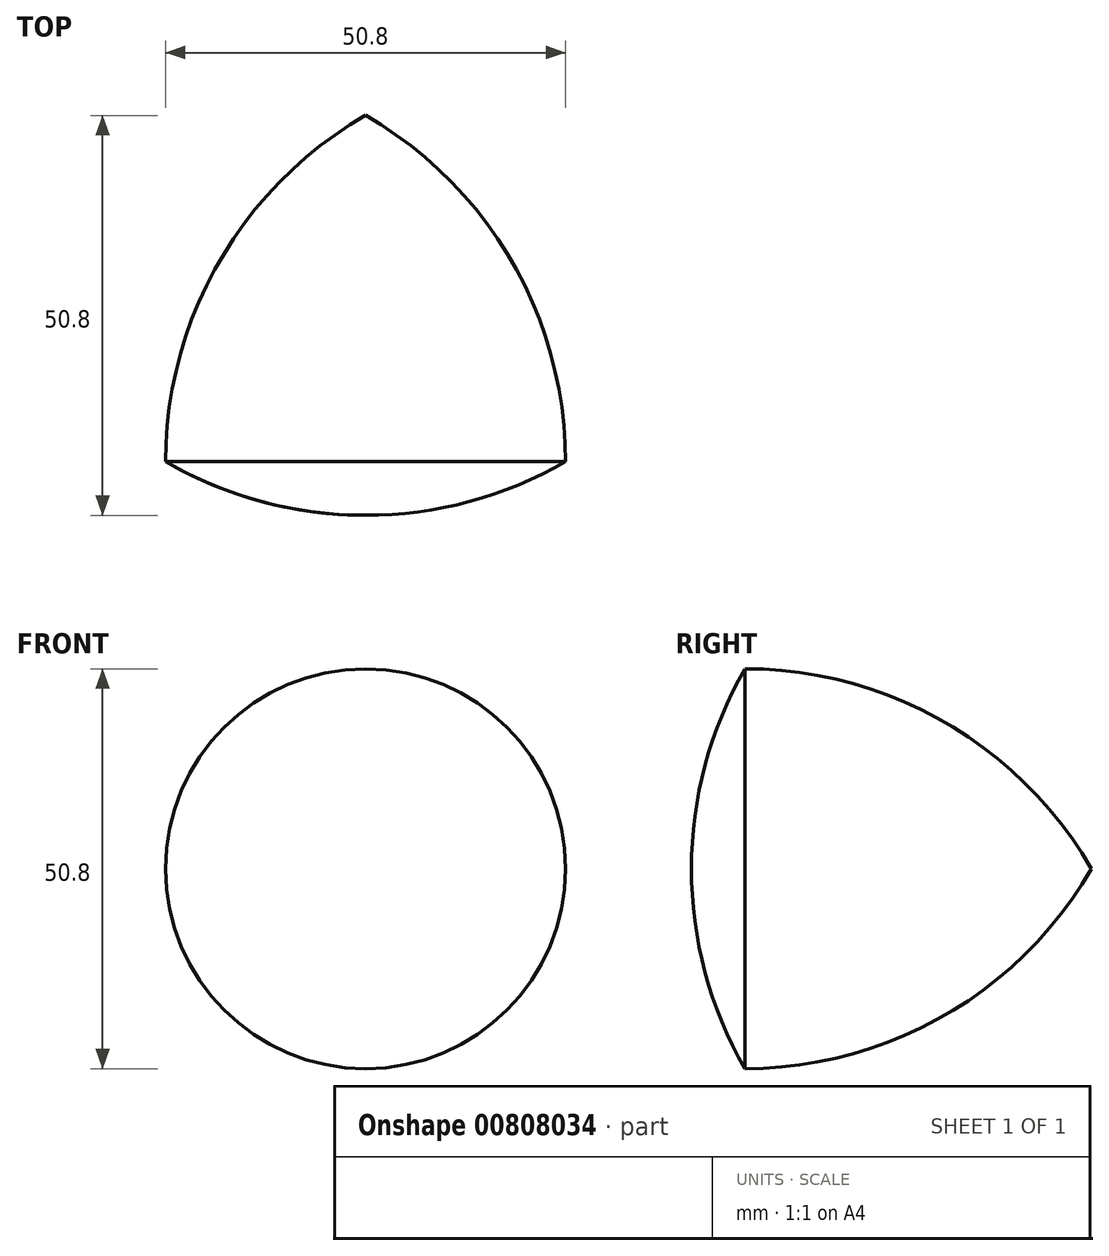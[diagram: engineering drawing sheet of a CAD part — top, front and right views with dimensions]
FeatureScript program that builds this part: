
annotation { "Feature Type Name" : "Feature", "Feature Type Description" : "" }
export const myFeature = defineFeature(function(context is Context, id is Id, definition is map)
    precondition{}
    {
        {
            var Q0;
            Q0=qCreatedBy(makeId("Top.planeOp"),FACE);
            var sketch = newSketch(context, id + "F0", { "sketchPlane" : qUnion([Q0])});
            skLineSegment(sketch, "E0", {"start": v(-25.4, 0) * mm, "end": v(25.4, 0) * mm});
            skLineSegment(sketch, "E1", {"start": v(25.4, 0) * mm, "end": v(0, 44) * mm});
            skLineSegment(sketch, "E2", {"start": v(0, 44) * mm, "end": v(-25.4, 0) * mm});
            skCircle(sketch, "E3", {"center": v(-25.4, 0) * mm, "radius": 50.8 * mm});
            skPoint(sketch, "E3.third.point", {"position": v(-71.73, -20.83) * mm});
            skCircle(sketch, "E4", {"center": v(25.4, 0) * mm, "radius": 50.8 * mm});
            skPoint(sketch, "E4.third.point", {"position": v(67.6, -28.28) * mm});
            skCircle(sketch, "E5", {"center": v(0, 44) * mm, "radius": 50.8 * mm});
            skPoint(sketch, "E5.third.point", {"position": v(0, 94.8) * mm});
            skCircle(sketch, "E6", {"center": v(0, 14.66) * mm, "radius": 29.33 * mm});
            skLineSegment(sketch, "E7", {"start": v(0, 44) * mm, "end": v(0, 0) * mm});
            skLineSegment(sketch, "E8", {"start": v(0, 44) * mm, "end": v(0, -6.8) * mm});
            skSolve(sketch);
        }
        {
            var Q0;
            {var subQ0=sQuery(id+"F0.wireOp",EDGE,"E2");Q0=makeQuery(id+"F0.imprint","IMPRINT",FACE,{"disambiguationData":[TD([[makeQuery(id+"F0.imprint","IMPRINT",EDGE,{"derivedFrom":subQ0}),-1.0]])]});}
            var Q1;
            {var subQ0=sQuery(id+"F0.wireOp",EDGE,"E2");Q1=makeQuery(id+"F0.imprint","IMPRINT",FACE,{"disambiguationData":[TD([[makeQuery(id+"F0.imprint","IMPRINT",EDGE,{"derivedFrom":subQ0}),1.0]])]});}
            var Q2;
            {var subQ2=sQuery(id+"F0.wireOp",EDGE,"E0");var subQ4=makeQuery(id+"F0.imprint","INTERSECT",VERTEX,{"derivedFrom":[subQ2,sQuery(id+"F0.wireOp",EDGE,"E7")]});Q2=makeQuery(id+"F0.imprint","IMPRINT",FACE,{"disambiguationData":[TD([[makeQuery(id+"F0.imprint","IMPRINT",EDGE,{"disambiguationData":[TD([[subQ4,1.0]])],"derivedFrom":subQ2}),-1.0]])]});}
            var Q3;
            Q3=sQuery(id+"F0.wireOp",EDGE,"E7");
            revolve(context, id + "F1", {"surfaceOperationType" : NewSurfaceOperationType.NEW, "entities" : qUnion([Q0, Q1, Q2]), "axis" : qUnion([Q3]), "revolveType" : RevolveType.FULL});
        }
    });
